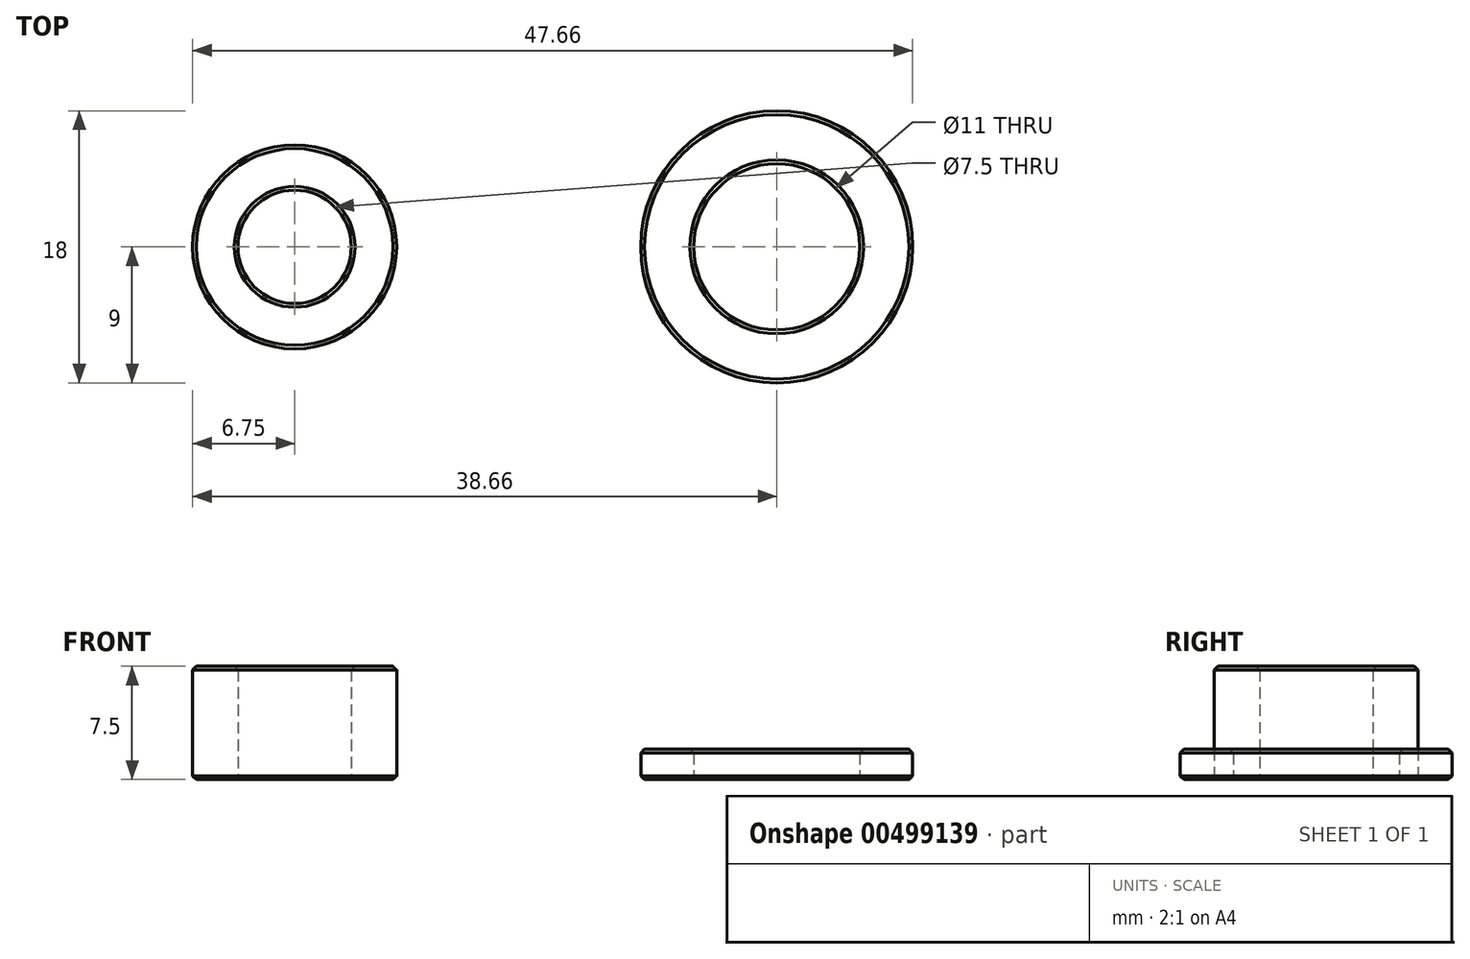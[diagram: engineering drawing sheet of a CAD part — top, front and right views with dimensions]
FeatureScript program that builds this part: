
annotation { "Feature Type Name" : "Feature", "Feature Type Description" : "" }
export const myFeature = defineFeature(function(context is Context, id is Id, definition is map)
    precondition{}
    {
        {
            var Q0;
            Q0=qCreatedBy(makeId("Top.planeOp"),FACE);
            var sketch = newSketch(context, id + "F0", { "sketchPlane" : qUnion([Q0])});
            skCircle(sketch, "E0", {"center": v(0, 0) * mm, "radius": 6.75 * mm});
            skCircle(sketch, "E1", {"center": v(0, 0) * mm, "radius": 3.75 * mm});
            skSolve(sketch);
        }
        {
            var Q0;
            Q0 = qSketchRegion(id + "F0", true);
            extrude(context, id + "F1", {"entities" : qUnion([Q0]), "depth" : 7.5 * mm});
        }
        {
            var Q0;
            Q0=qCreatedBy(makeId("Top.planeOp"),FACE);
            var sketch = newSketch(context, id + "F2", { "sketchPlane" : qUnion([Q0])});
            skCircle(sketch, "E2", {"center": v(31.9, 0) * mm, "radius": 9 * mm});
            skCircle(sketch, "E3", {"center": v(31.9, 0) * mm, "radius": 5.5 * mm});
            skSolve(sketch);
        }
        {
            var Q0;
            Q0 = qSketchRegion(id + "F2", true);
            extrude(context, id + "F3", {"entities" : qUnion([Q0]), "depth" : 2 * mm, "offsetDistance" : 25 * mm});
        }
        {
            var Q0;
            Q0=makeQuery(id+"F1.opExtrude","CAP_EDGE",EDGE,{"disambiguationData":[OSD([sQuery(id+"F0.wireOp",EDGE,"E0")])],"isStart":false});
            var Q1;
            Q1=makeQuery(id+"F1.opExtrude","CAP_EDGE",EDGE,{"disambiguationData":[OSD([sQuery(id+"F0.wireOp",EDGE,"E1")])],"isStart":false});
            var Q2;
            Q2=makeQuery(id+"F1.opExtrude","CAP_EDGE",EDGE,{"disambiguationData":[OSD([sQuery(id+"F0.wireOp",EDGE,"E0")])],"isStart":true});
            var Q3;
            Q3=makeQuery(id+"F1.opExtrude","CAP_EDGE",EDGE,{"disambiguationData":[OSD([sQuery(id+"F0.wireOp",EDGE,"E1")])],"isStart":true});
            var Q4;
            Q4=makeQuery(id+"F3.opExtrude","CAP_FACE",FACE,{"disambiguationData":[OSD([sQuery(id+"F2.wireOp",EDGE,"E2"),sQuery(id+"F2.wireOp",EDGE,"E3")])],"isStart":false});
            var Q5;
            Q5=makeQuery(id+"F3.opExtrude","CAP_EDGE",EDGE,{"disambiguationData":[OSD([sQuery(id+"F2.wireOp",EDGE,"E3")])],"isStart":true});
            var Q6;
            Q6=makeQuery(id+"F3.opExtrude","CAP_EDGE",EDGE,{"disambiguationData":[OSD([sQuery(id+"F2.wireOp",EDGE,"E2")])],"isStart":true});
            chamfer(context, id + "F4", {"entities" : qUnion([Q0, Q1, Q2, Q3, Q4, Q5, Q6]), "width" : .25 * mm, "tangentPropagation" : true});
        }
    });
